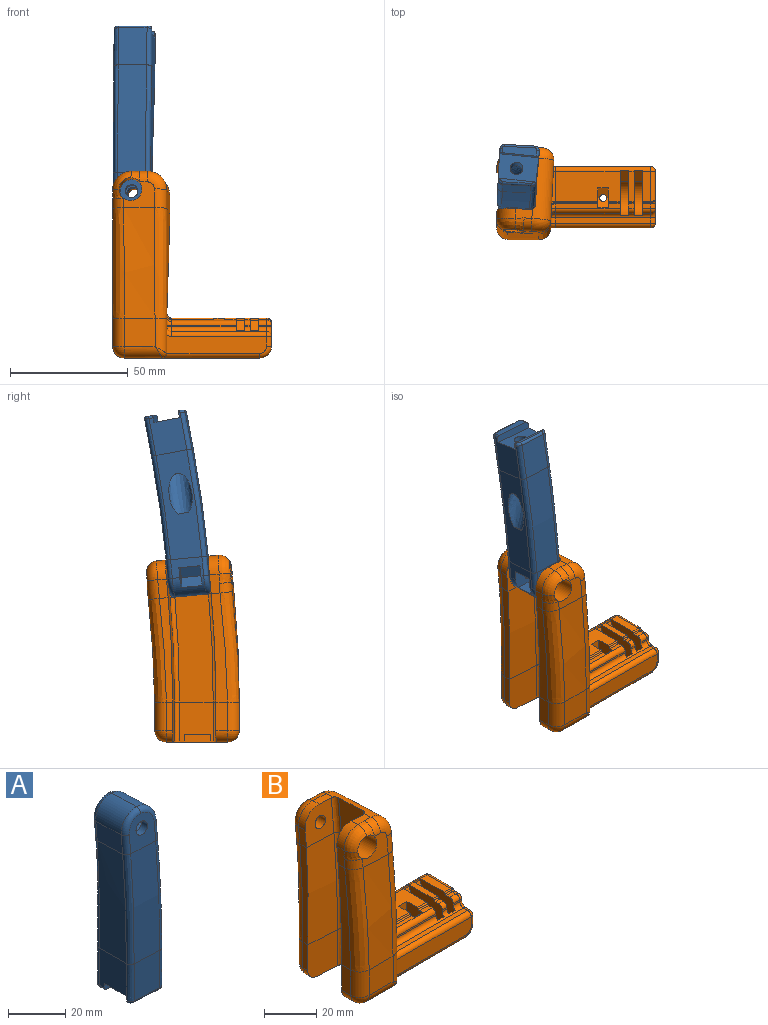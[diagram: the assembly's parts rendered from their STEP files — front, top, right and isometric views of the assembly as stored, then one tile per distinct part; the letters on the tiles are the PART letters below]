
ASSEMBLY  parts=2 mates=1
PART A: 57 faces, bbox 31.4x29.5x110.9 mm
  f0: plane 14.04x9.19mm, normal (1,-0.05,0), area 68.8mm2, adj f2,f27,f28,f29,f30,f36,f43
  f1: cylinder r=2.7mm len=5.85mm, axis (-0.05,-0.99,0.09), area 88.1mm2, adj f13,f29
  f2: offset ~46.61x20.29mm, area 470.7mm2, adj f0,f8,f21,f22,f34,f41
  f3: plane 14.8x3.53mm, normal (0,0,-1), area 46.8mm2, adj f16,f48,f49,f50,f51,f52
  f4: plane 14.09x1.41mm, normal (0,0,-1), area 15mm2, adj f15,f53,f54,f55,f56
  f5: plane 16x13.41mm, normal (-1,0,0), area 192.7mm2, adj f6,f16,f17,f33,f42,f48
  f6: bspline ~46.4x28.98mm, area 606.4mm2, adj f5,f7,f35,f44
  f7: plane 14.04x9.19mm, normal (-1,0.05,0), area 107.1mm2, adj f6,f31,f37,f46
  f8: plane 16x13.37mm, normal (1,-0.05,0), area 191.9mm2, adj f2,f15,f16,f17,f32,f40,f52,f56
  f9: plane 16.01x12.81mm, normal (0.05,1,0), area 205.1mm2, adj f11,f32,f33,f50
  f10: plane 16.01x12.1mm, normal (-0.05,-1,0), area 193.8mm2, adj f12,f40,f42,f54
  f11: offset ~44.97x22.27mm, area 546.9mm2, adj f9,f13,f34,f35
  f12: offset ~46.61x22.09mm, area 550mm2, adj f10,f14,f41,f44
  f13: plane 13.97x11.73mm, normal (0.05,0.99,-0.09), area 126.1mm2, adj f1,f11,f36,f37,f38,f39
  f14: plane 13.97x11.73mm, normal (-0.05,-0.99,0.09), area 126.1mm2, adj f12,f23,f43,f45,f46,f47
  f15: plane 16.24x3.13mm, normal (0,1,0), area 47.9mm2, adj f4,f8,f17,f42,f53,f56
  f16: plane 16.73x3.02mm, normal (0,-1,0), area 49.7mm2, adj f3,f5,f8,f17,f48,f52
  f17: plane 16.71x11.1mm, normal (0,0,-1), area 159.3mm2, adj f5,f8,f15,f16,f18,f42
  f18: cylinder r=2.7mm len=8mm, axis (0,0,-1), area 135.7mm2, adj f17,f20
  f19: cylinder r=4.88mm len=10mm, axis (0,0,-1), area 306.3mm2, adj f20,f22
  f20: plane 9.75x9.75mm, normal (0,0,1), area 51.8mm2, adj f18,f19
  f21: plane 4.95x1.01mm, normal (0,0,-1), area 1.9mm2, adj f2,f22
  f22: bspline ~22.2x21.54mm, area 461.4mm2, adj f2,f19,f21
  f23: cylinder r=2.7mm len=5.67mm, axis (-0.05,-0.99,0.09), area 54.2mm2, adj f14,f28
  f24: plane 9.57x9.43mm, normal (0,-0.09,-1), area 82mm2, adj f25,f28,f29,f30
  f25: plane 9.21x5.07mm, normal (0.86,-0.09,-0.49), area 44.2mm2, adj f24,f26,f28,f29
  f26: plane 9.47x5.04mm, normal (0.86,0,0.5), area 44.2mm2, adj f25,f27,f28,f29
  f27: plane 10.79x9.49mm, normal (0,0.09,1), area 93mm2, adj f0,f26,f28,f29
  f28: plane 12.76x8.51mm, normal (0.05,0.99,-0.09), area 73.6mm2, adj f0,f23,f24,f25,f26,f27,f30
  f29: plane 12.76x8.51mm, normal (-0.05,-0.99,0.09), area 73.6mm2, adj f0,f1,f24,f25,f26,f27,f30
  f30: cylinder r=8mm len=14.46mm, axis (0.05,0.99,-0.09), area 126.2mm2, adj f0,f24,f28,f29,f31,f38,f45
  f31: cylinder r=8mm len=13.73mm, axis (0.05,0.99,-0.09), area 166.5mm2, adj f7,f30,f39,f47
  f32: bspline ~32.83x2.1mm, area 50.3mm2, adj f8,f9,f34,f51
  f33: bspline ~36.43x2.29mm, area 52mm2, adj f5,f9,f35,f49
  f34: bspline ~52.18x4.18mm, area 140.2mm2, adj f2,f11,f32,f36
  f35: bspline ~49.11x4.08mm, area 142.3mm2, adj f6,f11,f33,f37
  f36: cylinder r=2mm len=8.16mm, axis (0,-0.09,-1), area 25.1mm2, adj f0,f13,f34,f38
  f37: cylinder r=2mm len=8.14mm, axis (0,-0.09,-1), area 25.1mm2, adj f7,f13,f35,f39
  f38: torus R=6mm, axis (0.05,0.99,-0.09), area 35.5mm2, adj f13,f30,f36,f39
  f39: torus R=6mm, axis (0.05,0.99,-0.09), area 35.5mm2, adj f13,f31,f37,f38
  f40: bspline ~25.29x2.1mm, area 50.3mm2, adj f8,f10,f41,f55
  f41: bspline ~50.86x4.21mm, area 144.7mm2, adj f2,f12,f40,f43
  f42: bspline ~56.73x2.01mm, area 48.1mm2, adj f5,f10,f15,f17,f44,f53
  f43: cylinder r=2mm len=8.14mm, axis (0,-0.09,-1), area 25.1mm2, adj f0,f14,f41,f45
  f44: bspline ~50.69x4.32mm, area 142.1mm2, adj f6,f12,f42,f46
  f45: torus R=6mm, axis (-0.05,-0.99,0.09), area 35.5mm2, adj f14,f30,f43,f47
  f46: cylinder r=2mm len=8.16mm, axis (0,0.09,1), area 25.1mm2, adj f7,f14,f44,f47
  f47: torus R=6mm, axis (-0.05,-0.99,0.09), area 35.5mm2, adj f14,f31,f45,f46
  f48: cylinder r=1mm len=2.53mm, axis (0,1,0), area 4mm2, adj f3,f5,f16,f49
  f49: torus R=1mm, axis (0,0,-1), area 4.2mm2, adj f3,f33,f48,f50
  f50: cylinder r=1mm len=12.86mm, axis (1,-0.05,0), area 20.1mm2, adj f3,f9,f49,f51
  f51: torus R=1mm, axis (0,0,-1), area 4mm2, adj f3,f32,f50,f52
  f52: cylinder r=1mm len=1.85mm, axis (-0.05,-1,0), area 2.8mm2, adj f3,f8,f16,f51
  f53: torus R=1mm, axis (0,0,-1), area 3.5mm2, adj f4,f15,f42,f54
  f54: cylinder r=1mm len=12.15mm, axis (-1,0.05,0), area 19mm2, adj f4,f10,f53,f55
  f55: torus R=1mm, axis (0,0,-1), area 4mm2, adj f4,f40,f54,f56
  f56: cylinder r=1mm len=1.03mm, axis (-0.05,-1,0), area 0.8mm2, adj f4,f8,f15,f55
PART B: 162 faces, bbox 83.3x49.8x96.8 mm
  f0: plane 12.8x2.5mm, normal (0,0,1), area 32mm2, adj f48,f66,f73,f143
  f1: plane 27.5x12.8mm, normal (0,0,1), area 326.1mm2, adj f41,f42,f67,f80,f81,f82,f125,f143
  f2: plane 12.98x11mm, normal (0.05,0.99,-0.09), area 92.6mm2, adj f16,f85,f86,f87,f88,f99,f100,f102
  f3: cylinder r=2.7mm len=5.81mm, axis (-0.05,-0.99,0.09), area 80.6mm2, adj f29,f91
  f4: plane 6.3x4.5mm, normal (1,0,0), area 14.6mm2, adj f13,f123,f133,f134,f136,f154
  f5: plane 7.24x4.13mm, normal (0,0.09,1), area 27mm2, adj f27,f35,f36,f97,f112,f114
  f6: plane 8.35x4.47mm, normal (-1,0.05,0), area 30.8mm2, adj f7,f27,f35,f111,f113
  f7: bspline ~46.85x34mm, area 202.2mm2, adj f6,f8,f24,f115
  f8: plane 12x4.98mm, normal (-1,0,0), area 59.8mm2, adj f7,f21,f117,f118
  f9: plane 26.48x10.33mm, normal (1,-0.05,0), area 207.1mm2, adj f13,f36,f105,f119
  f10: plane 12.98x11mm, normal (-0.05,-0.99,0.09), area 87mm2, adj f14,f34,f113,f114,f116,f119
  f11: plane 8.31x4.46mm, normal (-1,0.05,0), area 30mm2, adj f15,f29,f37,f99
  f12: plane 7.21x4.27mm, normal (0,0.09,1), area 26.3mm2, adj f29,f36,f37,f94,f100
  f13: bspline ~46.51x32.74mm, area 1141.4mm2, adj f4,f9,f107,f121,f125,f126,f131,f132
  f14: offset ~56.51x33.19mm, area 610.9mm2, adj f10,f18,f115,f121
  f15: bspline ~44.37x6.75mm, area 140.9mm2, adj f11,f19,f26,f101
  f16: offset ~54.14x34.46mm, area 567.9mm2, adj f2,f17,f101,f107
  f17: plane 13x12mm, normal (0,1,0), area 156mm2, adj f16,f103,f108,f109
  f18: plane 13x12mm, normal (0,-1,0), area 156mm2, adj f14,f118,f122,f123
  f19: plane 12x2.61mm, normal (-1,0,0), area 31.3mm2, adj f15,f22,f103,f104
  f20: plane 57.56x26.06mm, normal (0,0,-1), area 1080.9mm2, adj f21,f22,f23,f30,f31,f33,f83,f92
  f21: plane 17.11x14.57mm, normal (0.05,1,0), area 240.8mm2, adj f8,f20,f24,f95,f117
  f22: plane 17.11x15.55mm, normal (-0.05,-1,0), area 257.4mm2, adj f19,f20,f26,f92,f104
  f23: plane 17x14.37mm, normal (-1,0.05,0), area 211.2mm2, adj f20,f25,f30,f31,f32,f92,f95
  f24: offset ~46.61x22.34mm, area 662.9mm2, adj f7,f21,f27,f96
  f25: offset ~46.63x20.79mm, area 652.4mm2, adj f23,f28,f93,f96
  f26: offset ~44.97x22.74mm, area 660.4mm2, adj f15,f22,f29,f93
  f27: plane 16x14.23mm, normal (0.05,0.99,-0.09), area 139.6mm2, adj f5,f6,f24,f34,f35,f97
  f28: plane 17.15x15.76mm, normal (-1,0.05,0), area 228.7mm2, adj f25,f36,f94,f97
  f29: plane 16x14.23mm, normal (-0.05,-0.99,0.09), area 191.4mm2, adj f3,f11,f12,f26,f37,f94
  f30: plane 3x2.26mm, normal (0,1,0), area 6.8mm2, adj f20,f23,f32,f33
  f31: plane 3x1.67mm, normal (0,-1,0), area 5mm2, adj f20,f23,f32,f33
  f32: plane 11.1x2.26mm, normal (0,0,-1), area 21.8mm2, adj f23,f30,f31,f33
  f33: plane 11.1x3mm, normal (-1,0,0), area 33.3mm2, adj f20,f30,f31,f32
  f34: cylinder r=4.88mm len=10.51mm, axis (-0.05,-0.99,0.09), area 268.2mm2, adj f10,f27,f110,f111,f112
  f35: cylinder r=8mm len=8.39mm, axis (0.05,0.99,-0.09), area 52.1mm2, adj f5,f6,f27,f110
  f36: cylinder r=8mm len=26.9mm, axis (-0.05,-0.99,0.09), area 305mm2, adj f5,f9,f12,f28,f94,f97,f102,f116
  f37: cylinder r=8mm len=8.35mm, axis (0.05,0.99,-0.09), area 47.1mm2, adj f11,f12,f29,f98
  f38: plane 27.5x2mm, normal (0,0,1), area 47.1mm2, adj f39,f40,f51,f67,f77,f81,f82,f131
  f39: cylinder r=0.5mm len=18mm, axis (1,0,0), area 14.1mm2, adj f38,f41,f81,f130
  f40: cylinder r=0.5mm len=5mm, axis (1,0,0), area 3.9mm2, adj f38,f42,f67,f82
  f41: cylinder r=0.5mm len=18mm, axis (-1,0,0), area 14.1mm2, adj f1,f39,f81,f126,f127,f130
  f42: cylinder r=0.5mm len=5mm, axis (-1,0,0), area 3.9mm2, adj f1,f40,f67,f82
  f43: cylinder r=2.5mm len=20mm, axis (-1,0,0), area 314.2mm2, adj f81,f84
  f44: plane 12.8x3.5mm, normal (0,0,1), area 44.8mm2, adj f59,f72,f143,f146
  f45: plane 2.5x2mm, normal (0,0,1), area 5mm2, adj f47,f49,f66,f73
  f46: plane 2.5x0.75mm, normal (0,-1,0), area 1.9mm2, adj f49,f61,f66,f73
  f47: cylinder r=0.5mm len=2.5mm, axis (1,0,0), area 2mm2, adj f45,f48,f66,f73
  f48: cylinder r=0.5mm len=2.5mm, axis (-1,0,0), area 2mm2, adj f0,f47,f66,f73
  f49: cylinder r=2mm len=2.5mm, axis (-1,0,0), area 7.9mm2, adj f45,f46,f66,f73
  f50: plane 27.5x0.75mm, normal (0,-1,0), area 20.6mm2, adj f51,f61,f67,f134
  f51: cylinder r=2mm len=27.5mm, axis (-1,0,0), area 86.4mm2, adj f38,f50,f67,f132,f133
  f52: plane 42.5x7.79mm, normal (0,-1,0), area 306.5mm2, adj f123,f151,f153,f154,f156,f157
  f53: plane 42.5x13.54mm, normal (0,1,0), area 550.9mm2, adj f109,f140,f141,f142,f143,f144
  f54: plane 3.5x2mm, normal (0,0,1), area 7mm2, adj f58,f60,f72,f152
  f55: plane 3.5x0.75mm, normal (0,-1,0), area 2.6mm2, adj f60,f61,f72,f158
  f56: plane 40.5x2.2mm, normal (0,0,1), area 89.1mm2, adj f61,f136,f157,f161
  f57: plane 22x10mm, normal (1,0,0), area 164.8mm2, adj f75,f124,f144,f146,f150,f152,f156,f158
  f58: cylinder r=0.5mm len=3.5mm, axis (1,0,0), area 2.7mm2, adj f54,f59,f72,f150
  f59: cylinder r=0.5mm len=3.5mm, axis (-1,0,0), area 2.7mm2, adj f44,f58,f72,f148
  f60: cylinder r=2mm len=3.5mm, axis (-1,0,0), area 11mm2, adj f54,f55,f72,f155
  f61: cylinder r=2mm len=40.5mm, axis (1,0,0), area 112.6mm2, adj f46,f50,f55,f56,f62,f66,f67,f68
  f62: plane 3.5x3.02mm, normal (0,1,0), area 10.6mm2, adj f61,f63,f66,f67
  f63: cylinder r=7.5mm len=14.3mm, axis (-1,0,0), area 71mm2, adj f62,f64,f66,f67
  f64: plane 10.67x4.98mm, normal (0,-0.91,0.42), area 41.2mm2, adj f63,f65,f66,f67
  f65: plane 3.5x0.94mm, normal (0,-1,0), area 3.3mm2, adj f64,f66,f67,f143
  f66: plane 19.27x16mm, normal (-1,0,0), area 209.9mm2, adj f0,f45,f46,f47,f48,f49,f61,f62
  f67: plane 19.27x16mm, normal (1,0,0), area 209.9mm2, adj f1,f38,f40,f42,f50,f51,f61,f62
  f68: plane 3.5x3.02mm, normal (0,1,0), area 10.6mm2, adj f61,f69,f72,f73
  f69: cylinder r=7.5mm len=14.3mm, axis (-1,0,0), area 71mm2, adj f68,f70,f72,f73
  f70: plane 10.67x4.98mm, normal (0,-0.91,0.42), area 41.2mm2, adj f69,f71,f72,f73
  f71: plane 3.5x0.94mm, normal (0,-1,0), area 3.3mm2, adj f70,f72,f73,f143
  f72: plane 19.27x16mm, normal (-1,0,0), area 209.9mm2, adj f44,f54,f55,f58,f59,f60,f61,f68
  f73: plane 19.27x16mm, normal (1,0,0), area 209.9mm2, adj f0,f45,f46,f47,f48,f49,f61,f68
  f74: cylinder r=2.5mm len=5mm, axis (-1,0,0), area 39.3mm2, adj f66,f73
  f75: cylinder r=2.5mm len=5.5mm, axis (-1,0,0), area 86.4mm2, adj f57,f72
  f76: cylinder r=2.5mm len=5mm, axis (-1,0,0), area 78.5mm2, adj f67,f82
  f77: plane 9.95x4.5mm, normal (0,1,0), area 44.8mm2, adj f38,f78,f81,f82
  f78: plane 6.23x5.98mm, normal (0,0.5,0.87), area 18mm2, adj f77,f79,f81,f82,f83
  f79: plane 6.23x5.98mm, normal (0,-0.5,0.87), area 18mm2, adj f78,f80,f81,f82,f83
  f80: plane 10.95x4.5mm, normal (0,-1,0), area 49.3mm2, adj f1,f79,f81,f82
  f81: plane 13.41x8.5mm, normal (1,0,0), area 81.7mm2, adj f1,f38,f39,f41,f43,f77,f78,f79
  f82: plane 13.41x8.5mm, normal (-1,0,0), area 81.7mm2, adj f1,f38,f40,f42,f76,f77,f78,f79
  f83: cylinder r=1.5mm len=3.59mm, axis (0,0,1), area 33.9mm2, adj f20,f78,f79
  f84: plane 5x5mm, normal (1,0,0), area 19.6mm2, adj f43
  f85: plane 4.59x4.39mm, normal (-0.86,0,-0.5), area 19.6mm2, adj f2,f86,f90,f91,f100
  f86: plane 4.61x4.24mm, normal (-0.86,0.09,0.49), area 19.6mm2, adj f2,f85,f87,f91
  f87: plane 5.11x4.24mm, normal (0,0.09,1), area 19.6mm2, adj f2,f86,f88,f91
  f88: plane 4.67x4.26mm, normal (0.86,0,0.5), area 19.1mm2, adj f2,f87,f89,f91,f99
  f89: plane 4.57x3.95mm, normal (0.86,-0.09,-0.49), area 18.4mm2, adj f88,f90,f91,f98
  f90: plane 5.52x4.38mm, normal (0,-0.09,-1), area 18.7mm2, adj f85,f89,f91,f98,f100
  f91: plane 9.8x8.49mm, normal (0.05,0.99,-0.09), area 39.7mm2, adj f3,f85,f86,f87,f88,f89,f90
  f92: bspline ~37.17x2.29mm, area 53.4mm2, adj f20,f22,f23,f93
  f93: bspline ~47.5x4.17mm, area 140mm2, adj f25,f26,f92,f94
  f94: bspline ~16.13x3.56mm, area 50.2mm2, adj f12,f28,f29,f36,f93
  f95: bspline ~17x2.1mm, area 53.4mm2, adj f20,f21,f23,f96
  f96: bspline ~49.21x4.14mm, area 144.9mm2, adj f24,f25,f95,f97
  f97: bspline ~30.73x4.8mm, area 50.2mm2, adj f5,f27,f28,f36,f96
  f98: torus R=3mm, axis (0.05,0.99,-0.09), area 66.6mm2, adj f37,f89,f90,f99,f100
  f99: cylinder r=5mm len=8.4mm, axis (0,0.09,1), area 59.1mm2, adj f2,f11,f88,f98,f101
  f100: cylinder r=5mm len=7.26mm, axis (1,-0.05,0), area 51.6mm2, adj f2,f12,f85,f90,f98,f102
  f101: bspline ~53.59x8.77mm, area 344.8mm2, adj f15,f16,f99,f103
  f102: torus R=3mm, axis (0.05,0.99,-0.09), area 76.3mm2, adj f2,f36,f100,f105
  f103: cylinder r=5mm len=12mm, axis (0,0,-1), area 94.2mm2, adj f17,f19,f101,f106
  f104: cylinder r=5mm len=5mm, axis (0,1,0), area 21.5mm2, adj f19,f20,f22,f106
  f105: cylinder r=5mm len=8.45mm, axis (0,-0.09,-1), area 62.8mm2, adj f2,f9,f102,f107
  f106: sphere r=5mm, area 53.5mm2, adj f103,f104,f108
  f107: bspline ~53.71x7.07mm, area 344.9mm2, adj f13,f16,f105,f109,f139
  f108: cylinder r=5mm len=16mm, axis (1,0,0), area 113.9mm2, adj f17,f20,f106,f137
  f109: cylinder r=5mm len=15mm, axis (0,0,-1), area 106mm2, adj f17,f53,f107,f137,f139
  f110: bspline ~8x7.99mm, area 64mm2, adj f34,f35,f111,f112
  f111: bspline ~5.29x5.18mm, area 25.5mm2, adj f6,f34,f110,f113
  f112: bspline ~5.47x5.18mm, area 24.2mm2, adj f5,f34,f110,f114
  f113: cylinder r=5mm len=5.61mm, axis (0,-0.09,-1), area 31.9mm2, adj f6,f10,f111,f115
  f114: cylinder r=5mm len=5.6mm, axis (-1,0.05,0), area 25.8mm2, adj f5,f10,f112,f116
  f115: bspline ~62.88x8.97mm, area 367.7mm2, adj f7,f14,f113,f118
  f116: torus R=3mm, axis (0.05,0.99,-0.09), area 76.3mm2, adj f10,f36,f114,f119
  f117: cylinder r=5mm len=5mm, axis (0,1,0), area 38.1mm2, adj f8,f20,f21,f120
  f118: cylinder r=5mm len=12mm, axis (0,0,1), area 94.2mm2, adj f8,f18,f115,f120
  f119: cylinder r=5mm len=8.4mm, axis (0,0.09,1), area 62.8mm2, adj f9,f10,f116,f121
  f120: sphere r=5mm, area 39.3mm2, adj f117,f118,f122
  f121: bspline ~62.94x7.75mm, area 368mm2, adj f13,f14,f119,f123
  f122: cylinder r=5mm len=16mm, axis (-1,0,0), area 113.9mm2, adj f18,f20,f120,f147
  f123: cylinder r=5mm len=15mm, axis (0,0,1), area 113.2mm2, adj f4,f18,f52,f121,f147,f154
  f124: cylinder r=5mm len=22mm, axis (0,1,0), area 172.8mm2, adj f20,f57,f142,f153
  f125: bspline ~24.29x2.02mm, area 42.2mm2, adj f1,f13,f126,f139,f141
  f126: bspline ~2.85x2.51mm, area 4.5mm2, adj f13,f41,f125,f127,f128
  f127: torus R=2.5mm, axis (-1,0,0), area 0.1mm2, adj f41,f126,f129
  f128: bspline ~1.85x1.35mm, area 0.4mm2, adj f126,f129,f131
  f129: bspline ~1.96x0.9mm, area 0.9mm2, adj f127,f128,f130,f131
  f130: bspline ~0.5x0.5mm, area 0mm2, adj f39,f41,f129,f131
  f131: bspline ~12.14x2mm, area 5mm2, adj f13,f38,f128,f129,f130,f132
  f132: bspline ~4.15x2.83mm, area 6.2mm2, adj f13,f51,f131,f133
  f133: torus R=4mm, axis (-1,0,0), area 7.3mm2, adj f4,f51,f132,f134
  f134: cylinder r=2mm len=2mm, axis (0,0,-1), area 2.4mm2, adj f4,f50,f133,f135
  f135: sphere r=2mm, area 8.6mm2, adj f61,f134,f136
  f136: cylinder r=2mm len=2.2mm, axis (0,-1,0), area 6.9mm2, adj f4,f56,f135,f154
  f137: bspline ~5.91x5mm, area 16.7mm2, adj f108,f109,f138
  f138: torus R=3mm, axis (0,0,-1), area 4.5mm2, adj f20,f137,f140
  f139: bspline ~3.69x2.1mm, area 3.5mm2, adj f13,f107,f109,f125,f141
  f140: cylinder r=2mm len=42.26mm, axis (1,0,0), area 128.4mm2, adj f20,f53,f138,f142
  f141: bspline ~3.06x2.44mm, area 4.5mm2, adj f53,f125,f139,f143
  f142: torus R=3mm, axis (0,1,0), area 21.1mm2, adj f53,f124,f140,f144
  f143: cylinder r=2mm len=40.49mm, axis (-1,0,0), area 123.9mm2, adj f0,f1,f44,f53,f65,f66,f67,f71
  f144: cylinder r=2mm len=10mm, axis (0,0,1), area 31.4mm2, adj f53,f57,f142,f145
  f145: sphere r=2mm, area 8.6mm2, adj f143,f144,f146
  f146: cylinder r=2mm len=12.8mm, axis (0,-1,0), area 38.6mm2, adj f44,f57,f145,f148
  f147: bspline ~5.23x5mm, area 10.8mm2, adj f122,f123,f149
  f148: bspline ~2x2mm, area 1mm2, adj f59,f146,f150
  f149: torus R=3mm, axis (0,0,-1), area 4.5mm2, adj f20,f147,f151
  f150: torus R=2.5mm, axis (1,0,0), area 4.5mm2, adj f57,f58,f148,f152
  f151: cylinder r=2mm len=42.26mm, axis (-1,0,0), area 128.4mm2, adj f20,f52,f149,f153
  f152: cylinder r=2mm len=2mm, axis (0,-1,0), area 6.3mm2, adj f54,f57,f150,f155
  f153: torus R=3mm, axis (0,1,0), area 21.1mm2, adj f52,f124,f151,f156
  f154: torus R=4mm, axis (0,1,0), area 7.6mm2, adj f4,f52,f123,f136,f157
  f155: sphere r=2mm, area 6.3mm2, adj f60,f152,f158
  f156: cylinder r=2mm len=4.25mm, axis (0,0,-1), area 13.4mm2, adj f52,f57,f153,f159
  f157: cylinder r=2mm len=40.5mm, axis (1,0,0), area 127.2mm2, adj f52,f56,f154,f159
  f158: cylinder r=2mm len=2mm, axis (0,0,-1), area 2.4mm2, adj f55,f57,f155,f160
  f159: sphere r=2mm, area 6.3mm2, adj f156,f157,f161
  f160: torus R=4mm, axis (1,0,0), area 13.5mm2, adj f57,f61,f158,f161
  f161: cylinder r=2mm len=2.2mm, axis (0,-1,0), area 6.9mm2, adj f56,f57,f159,f160
PLACE A rot(axis=(-0.05,-0.99,0.09),180deg) t=(-87.52,15.94,122.65)mm
PLACE B at identity fixed
MATE revolute A.f1 <-> B.f34  axis (-0.05,-0.99,0.09) through (-44.44,-4.91,62.51)mm
